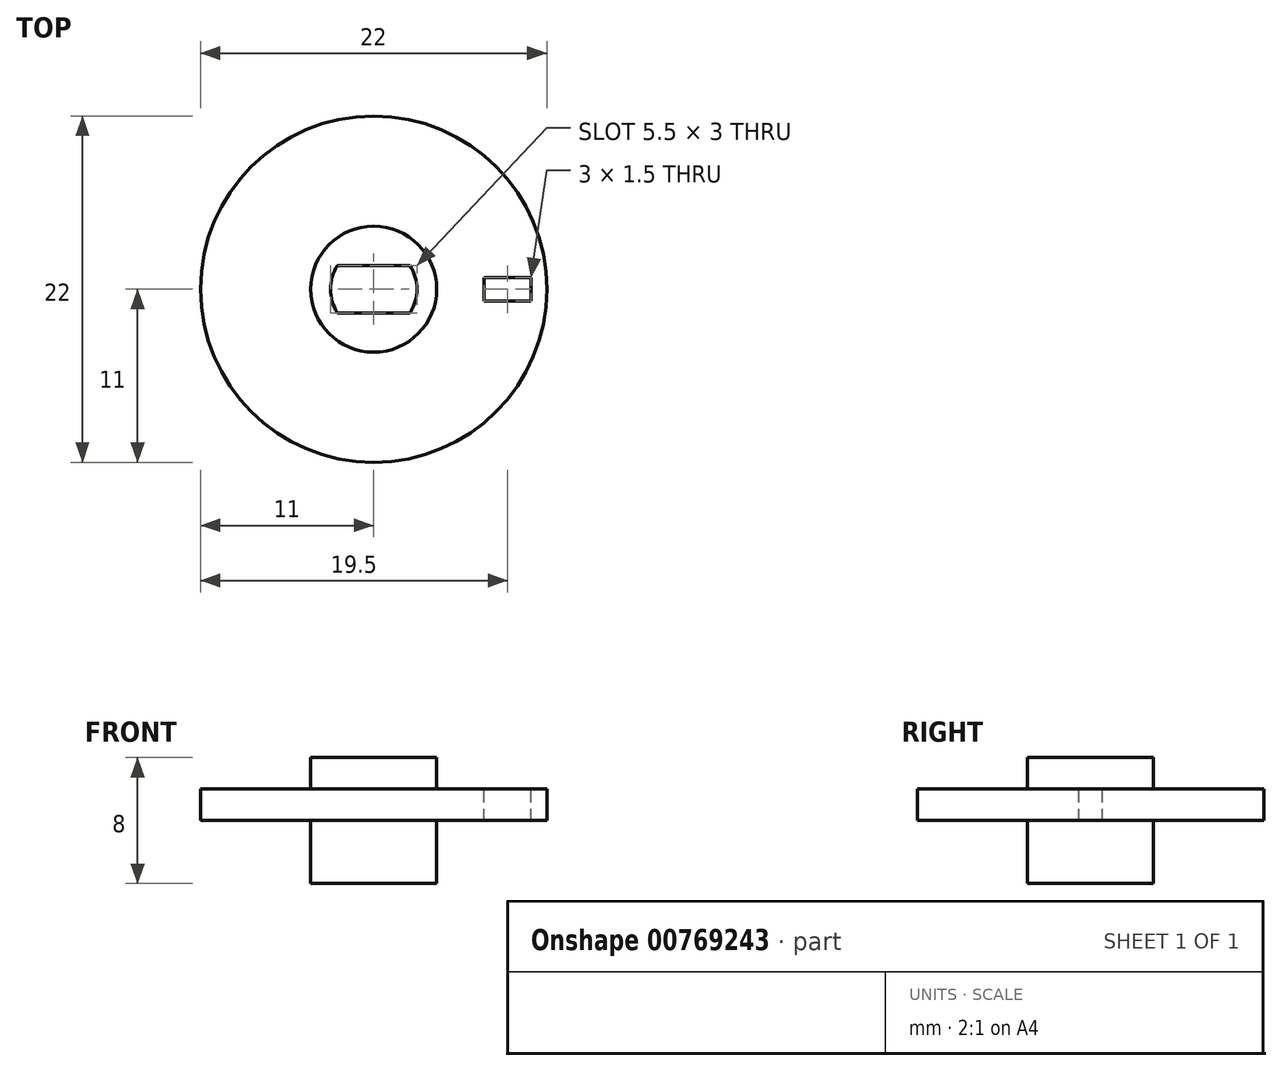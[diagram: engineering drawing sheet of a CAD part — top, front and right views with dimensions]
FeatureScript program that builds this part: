
annotation { "Feature Type Name" : "Feature", "Feature Type Description" : "" }
export const myFeature = defineFeature(function(context is Context, id is Id, definition is map)
    precondition{}
    {
        {
            var Q0;
            Q0=qCreatedBy(makeId("Top.planeOp"),FACE);
            var sketch = newSketch(context, id + "F0", { "sketchPlane" : qUnion([Q0])});
            skCircle(sketch, "E0", {"center": v(0, 0) * mm, "radius": 11 * mm});
            skSolve(sketch);
        }
        {
            var Q0;
            Q0=makeQuery(id+"F0.imprint","IMPRINT",FACE,{"disambiguationData":[TD([[makeQuery(id+"F0.imprint","IMPRINT",EDGE,{"derivedFrom":sQuery(id+"F0.wireOp",EDGE,"E0")}),1.0]])]});
            extrude(context, id + "F1", {"entities" : qUnion([Q0]), "depth" : 2 * mm, "offsetDistance" : 25 * mm});
        }
        {
            var Q0;
            Q0=makeQuery(id+"F1.opExtrude","CAP_FACE",FACE,{"disambiguationData":[OSD([sQuery(id+"F0.wireOp",EDGE,"E0")])],"isStart":false});
            var sketch = newSketch(context, id + "F2", { "sketchPlane" : qUnion([Q0])});
            skLineSegment(sketch, "E1.bottom", {"start": v(7, 0.75) * mm, "end": v(10, 0.75) * mm});
            skLineSegment(sketch, "E1.top", {"start": v(7, -0.75) * mm, "end": v(10, -0.75) * mm});
            skLineSegment(sketch, "E1.left", {"start": v(7, 0.75) * mm, "end": v(7, -0.75) * mm});
            skLineSegment(sketch, "E1.right", {"start": v(10, 0.75) * mm, "end": v(10, -0.75) * mm});
            skSolve(sketch);
        }
        {
            var Q0;
            Q0=qSketchRegion(id+"F2",true);
            extrude(context, id + "F3", {"entities" : qUnion([Q0]), "operationType" : NewBodyOperationType.REMOVE, "oppositeDirection" : true, "depth" : 2 * mm, "offsetDistance" : 25 * mm});
        }
        {
            var Q0;
            Q0=makeQuery(id+"F1.opExtrude","CAP_FACE",FACE,{"disambiguationData":[OSD([sQuery(id+"F0.wireOp",EDGE,"E0")])],"isStart":true});
            var sketch = newSketch(context, id + "F4", { "sketchPlane" : qUnion([Q0])});
            skCircle(sketch, "E2", {"center": v(0, 0) * mm, "radius": 4 * mm});
            skSolve(sketch);
        }
        {
            var Q0;
            Q0=qSketchRegion(id+"F4",true);
            extrude(context, id + "F5", {"entities" : qUnion([Q0]), "operationType" : NewBodyOperationType.ADD, "depth" : 4 * mm, "offsetDistance" : 25 * mm, "hasSecondDirection" : true, "secondDirectionOppositeDirection" : true, "secondDirectionDepth" : 4 * mm});
        }
        {
            var Q0;
            Q0=makeQuery(id+"F5.opExtrude","CAP_FACE",FACE,{"disambiguationData":[OSD([sQuery(id+"F4.wireOp",EDGE,"E2")])],"isStart":true});
            var sketch = newSketch(context, id + "F6", { "sketchPlane" : qUnion([Q0])});
            skArc(sketch, "E3", {"start": v(2.3, -1.5) * mm, "mid": v(2.75, 0) * mm, "end": v(2.3, 1.5) * mm});
            skArc(sketch, "E4", {"start": v(-2.3, 1.5) * mm, "mid": v(-2.75, 0) * mm, "end": v(-2.3, -1.5) * mm});
            skLineSegment(sketch, "E5", {"start": v(-2.3, 1.5) * mm, "end": v(2.3, 1.5) * mm});
            skLineSegment(sketch, "E6", {"start": v(2.3, -1.5) * mm, "end": v(-2.3, -1.5) * mm});
            skSolve(sketch);
        }
        {
            var Q0;
            Q0=qSketchRegion(id+"F6",true);
            extrude(context, id + "F7", {"entities" : qUnion([Q0]), "operationType" : NewBodyOperationType.REMOVE, "oppositeDirection" : true, "depth" : 9 * mm, "offsetDistance" : 25 * mm});
        }
    });
